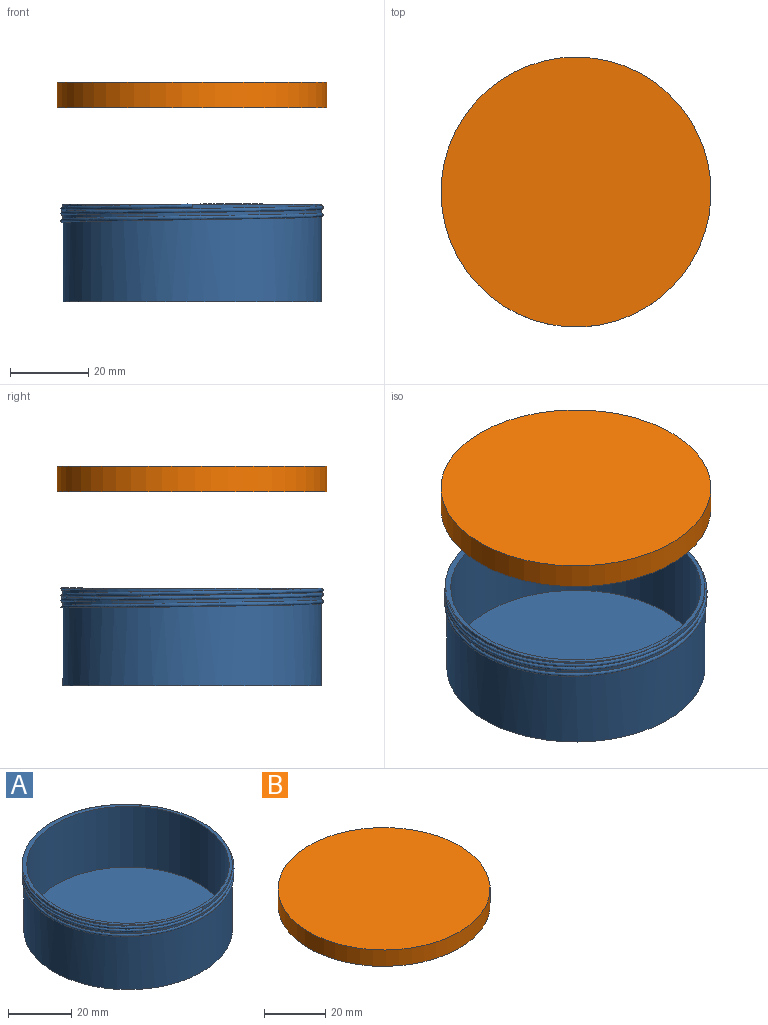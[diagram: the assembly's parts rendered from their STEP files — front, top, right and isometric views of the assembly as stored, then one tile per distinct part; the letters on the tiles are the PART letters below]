
ASSEMBLY  parts=2 mates=1
PART A: 12 faces, bbox 79.3x68.7x27.1 mm
  f0: bspline ~78.52x68mm, area 493.3mm2, adj f1,f3,f4,f6
  f1: cylinder r=33mm len=66mm, axis (0,0,1), area 4507.6mm2, adj f0,f2,f3,f4,f5,f6,f7,f8
  f2: cylinder r=33mm len=24.7mm, axis (0,0,1), area 5.5mm2, adj f1,f5,f8
  f3: cylinder r=33mm len=66mm, axis (0,0,1), area 107mm2, adj f0,f1,f5,f8
  f4: plane 57.74x17.57mm, normal (0,0,-1), area 27.3mm2, adj f0,f1
  f5: plane 67.23x66.75mm, normal (0,0,1), area 231.5mm2, adj f1,f2,f3,f8,f10
  f6: plane 1.14x0.64mm, normal (1,0,0), area 0.4mm2, adj f0,f1
  f7: plane 1.14x0.57mm, normal (0.5,-0.87,0), area 0.4mm2, adj f1,f8
  f8: bspline ~78.52x68mm, area 400.8mm2, adj f1,f2,f3,f5,f7
  f9: plane 66x66mm, normal (0,0,-1), area 3421.2mm2, adj f1
  f10: cylinder r=32mm len=64mm, axis (0,0,1), area 4725mm2, adj f5,f11
  f11: plane 64x64mm, normal (0,0,1), area 3217mm2, adj f10
PART B: 9 faces, bbox 77.4x69x6.6 mm
  f0: cylinder r=33.5mm len=67mm, axis (0,0,1), area 813.2mm2, adj f1,f4,f5,f6,f8
  f1: plane 69x69mm, normal (0,0,-1), area 213.6mm2, adj f0,f2,f7
  f2: cylinder r=34.5mm len=69mm, axis (0,0,1), area 1409mm2, adj f1,f3
  f3: plane 69x69mm, normal (0,0,1), area 3739.3mm2, adj f2
  f4: plane 0.58x0.5mm, normal (1,0,0), area 0.2mm2, adj f0,f5,f8
  f5: bspline ~77.37x67mm, area 532.6mm2, adj f0,f4,f6,f7,f8
  f6: plane 1x0.43mm, normal (0.5,-0.87,0), area 0.4mm2, adj f0,f5,f7
  f7: cylinder r=33.5mm len=4.56mm, axis (0,0,-1), area 0.2mm2, adj f1,f5,f6
  f8: plane 67x67mm, normal (0,0,-1), area 3514.6mm2, adj f0,f4,f5
PLACE A t=(-0.39,-0.08,11.96)mm fixed
PLACE B rot(axis=(0,0,1),4.7deg) t=(-0.39,-0.08,41.64)mm
MATE cylindrical B.f0 <-> A.f1  axis (0,0,-1) through (-0.39,-0.08,36.64)mm
